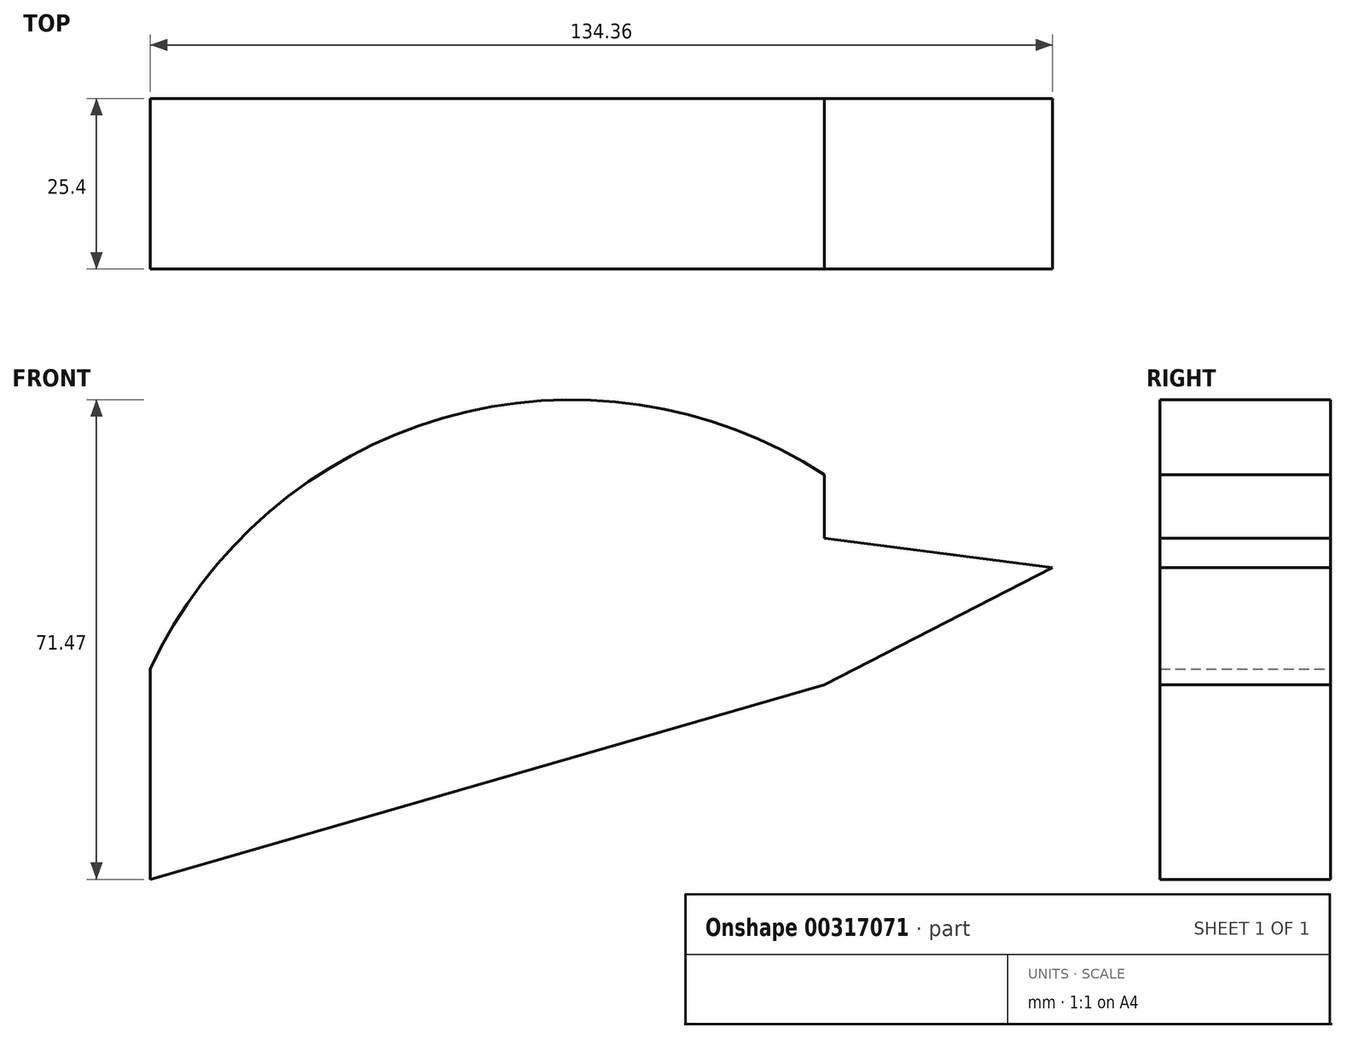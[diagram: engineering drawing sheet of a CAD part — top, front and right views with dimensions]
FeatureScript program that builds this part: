
annotation { "Feature Type Name" : "Feature", "Feature Type Description" : "" }
export const myFeature = defineFeature(function(context is Context, id is Id, definition is map)
    precondition{}
    {
        {
            var Q0;
            Q0=qCreatedBy(makeId("Front.planeOp"),FACE);
            var sketch = newSketch(context, id + "F0", { "sketchPlane" : qUnion([Q0])});
            skLineSegment(sketch, "E0", {"start": v(-64.86, 13.7) * mm, "end": v(35.52, 42.69) * mm});
            skLineSegment(sketch, "E1", {"start": v(-64.86, 13.7) * mm, "end": v(-64.86, -17.63) * mm});
            skLineSegment(sketch, "E2", {"start": v(-64.86, -17.63) * mm, "end": v(35.52, 11.35) * mm});
            skLineSegment(sketch, "E3", {"start": v(35.52, 42.69) * mm, "end": v(35.52, 11.35) * mm});
            skLineSegment(sketch, "E4", {"start": v(35.52, 33.2) * mm, "end": v(69.5, 28.81) * mm});
            skLineSegment(sketch, "E5", {"start": v(35.52, 11.35) * mm, "end": v(69.5, 28.81) * mm});
            skArc(sketch, "E6", {"start": v(35.52, 42.69) * mm, "mid": v(-21.3, 51.13) * mm, "end": v(-64.86, 13.7) * mm});
            skSolve(sketch);
        }
        {
            var Q0;
            Q0 = qSketchRegion(id + "F0", true);
            extrude(context, id + "F1", {"entities" : qUnion([Q0]), "depth" : 25.4 * mm});
        }
    });
